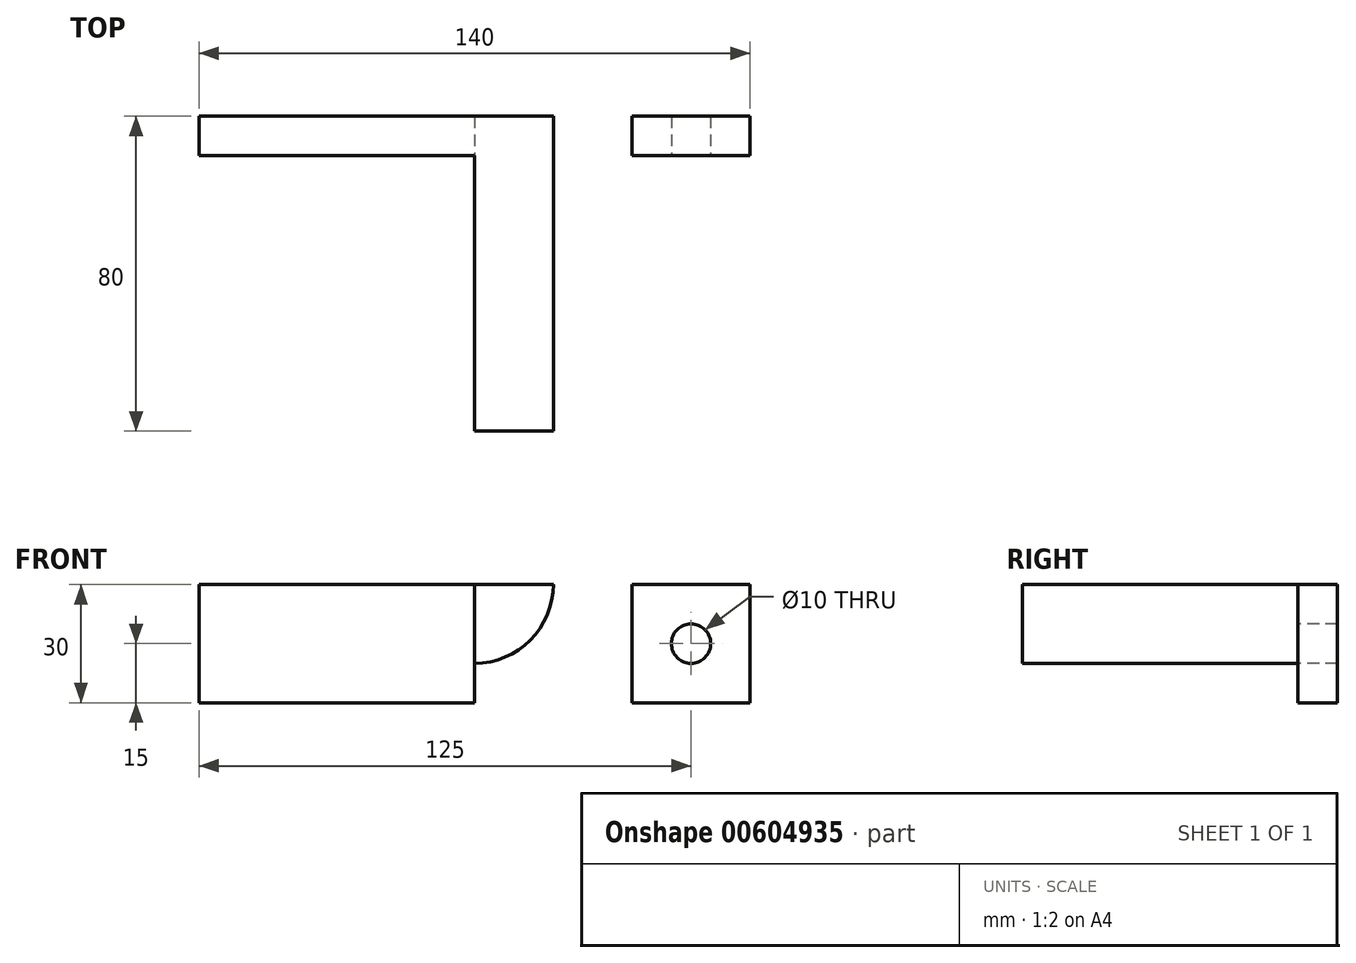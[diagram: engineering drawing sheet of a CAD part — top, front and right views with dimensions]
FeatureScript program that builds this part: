
annotation { "Feature Type Name" : "Feature", "Feature Type Description" : "" }
export const myFeature = defineFeature(function(context is Context, id is Id, definition is map)
    precondition{}
    {
        {
            var Q0;
            Q0=qCreatedBy(makeId("Right.planeOp"),FACE);
            var sketch = newSketch(context, id + "F0", { "sketchPlane" : qUnion([Q0])});
            skLineSegment(sketch, "E0", {"start": v(0, 30) * mm, "end": v(0, 0) * mm});
            skLineSegment(sketch, "E1", {"start": v(0, 0) * mm, "end": v(-60, 0) * mm});
            skLineSegment(sketch, "E2", {"start": v(-60, 0) * mm, "end": v(-60, -30) * mm});
            skLineSegment(sketch, "E3", {"start": v(-60, -30) * mm, "end": v(10, -30) * mm, "construction": true});
            skLineSegment(sketch, "E4", {"start": v(10, -30) * mm, "end": v(10, 30) * mm});
            skLineSegment(sketch, "E5", {"start": v(0, 30) * mm, "end": v(10, 30) * mm});
            skArc(sketch, "E6", {"start": v(-45, -30) * mm, "mid": v(-25, -10) * mm, "end": v(-5, -30) * mm});
            skLineSegment(sketch, "E7", {"start": v(-60, -30) * mm, "end": v(-45, -30) * mm, "construction": true});
            skLineSegment(sketch, "E8", {"start": v(-5, -30) * mm, "end": v(10, -30) * mm, "construction": true});
            skLineSegment(sketch, "E9", {"start": v(-60, -30) * mm, "end": v(-45, -30) * mm});
            skLineSegment(sketch, "E10", {"start": v(-5, -30) * mm, "end": v(10, -30) * mm});
            skSolve(sketch);
        }
        {
            var Q0;
            Q0=makeQuery(id+"F0.imprint","IMPRINT",FACE,{"disambiguationData":[TD([[makeQuery(id+"F0.imprint","IMPRINT",EDGE,{"derivedFrom":sQuery(id+"F0.wireOp",EDGE,"E0")}),1.0]])]});
            extrude(context, id + "F1", {"entities" : qUnion([Q0]), "endBound" : BoundingType.SYMMETRIC, "depth" : 140 * mm, "offsetDistance" : 25 * mm});
        }
        {
            var Q0;
            Q0=makeQuery(id+"F1.opExtrude","SWEPT_FACE",FACE,{"disambiguationData":[OSD([sQuery(id+"F0.wireOp",EDGE,"E0")])]});
            var sketch = newSketch(context, id + "F2", { "sketchPlane" : qUnion([Q0])});
            skLineSegment(sketch, "E11.bottom", {"start": v(40, 0) * mm, "end": v(0, 0) * mm});
            skLineSegment(sketch, "E11.top", {"start": v(40, 30) * mm, "end": v(0, 30) * mm});
            skLineSegment(sketch, "E11.left", {"start": v(40, 0) * mm, "end": v(40, 30) * mm});
            skLineSegment(sketch, "E11.right", {"start": v(0, 0) * mm, "end": v(0, 30) * mm});
            skSolve(sketch);
        }
        {
            var Q0;
            Q0=makeQuery(id+"F2.imprint","IMPRINT",FACE,{"disambiguationData":[TD([[makeQuery(id+"F2.imprint","IMPRINT",EDGE,{"derivedFrom":sQuery(id+"F2.wireOp",EDGE,"E11.bottom")}),-1.0]])]});
            extrude(context, id + "F3", {"entities" : qUnion([Q0]), "operationType" : NewBodyOperationType.ADD, "depth" : 60 * mm, "offsetDistance" : 25 * mm});
        }
        {
            var Q0;
            {var subQ0=sQuery(id+"F2.wireOp",EDGE,"E11.right");var subQ1=sQuery(id+"F2.wireOp",EDGE,"E11.left");var subQ2=sQuery(id+"F2.wireOp",EDGE,"E11.top");var subQ3=sQuery(id+"F2.wireOp",EDGE,"E11.bottom");Q0=makeQuery(id+"FlGcxx7yue9F5qh_1.1.F3.boolean.opBoolean","MERGE",FACE,{"derivedFrom":[makeQuery(id+"F3.boolean.opBoolean","MERGE",FACE,{"derivedFrom":[makeQuery(id+"F1.opExtrude","SWEPT_FACE",FACE,{"disambiguationData":[OSD([sQuery(id+"F0.wireOp",EDGE,"E2")])]}),makeQuery(id+"F3.opExtrude","CAP_FACE",FACE,{"disambiguationData":[OSD([subQ3,subQ2,subQ1,subQ0])],"isStart":false})]}),makeQuery(id+"FlGcxx7yue9F5qh_1.1.F3.opExtrude","CAP_FACE",FACE,{"disambiguationData":[OSD([subQ3,subQ2,subQ1,subQ0])],"isStart":false})]});}
            var sketch = newSketch(context, id + "F4", { "sketchPlane" : qUnion([Q0])});
            skArc(sketch, "E12", {"start": v(20, 30) * mm, "mid": v(0, 10) * mm, "end": v(-20, 30) * mm});
            skSolve(sketch);
        }
        {
            var Q0;
            {var subQ0=sQuery(id+"F4.wireOp",EDGE,"E12");Q0=makeQuery(id+"F4.imprint","IMPRINT",FACE,{"disambiguationData":[TD([[makeQuery(id+"F4.imprint","IMPRINT",EDGE,{"derivedFrom":subQ0}),-1.0]])]});}
            extrude(context, id + "F5", {"entities" : qUnion([Q0]), "operationType" : NewBodyOperationType.REMOVE, "endBound" : BoundingType.THROUGH_ALL, "oppositeDirection" : true, "depth" : 25 * mm, "offsetDistance" : 25 * mm});
        }
        {
            var Q0;
            {var subQ0=sQuery(id+"F2.wireOp",EDGE,"E11.right");var subQ1=sQuery(id+"F2.wireOp",EDGE,"E11.left");var subQ2=sQuery(id+"F2.wireOp",EDGE,"E11.top");var subQ3=sQuery(id+"F2.wireOp",EDGE,"E11.bottom");Q0=makeQuery(id+"FlGcxx7yue9F5qh_1.1.F3.boolean.opBoolean","MERGE",FACE,{"derivedFrom":[makeQuery(id+"F3.boolean.opBoolean","MERGE",FACE,{"derivedFrom":[makeQuery(id+"F1.opExtrude","SWEPT_FACE",FACE,{"disambiguationData":[OSD([sQuery(id+"F0.wireOp",EDGE,"E2")])]}),makeQuery(id+"F3.opExtrude","CAP_FACE",FACE,{"disambiguationData":[OSD([subQ3,subQ2,subQ1,subQ0])],"isStart":false})]}),makeQuery(id+"FlGcxx7yue9F5qh_1.1.F3.opExtrude","CAP_FACE",FACE,{"disambiguationData":[OSD([subQ3,subQ2,subQ1,subQ0])],"isStart":false})]});}
            var sketch = newSketch(context, id + "F6", { "sketchPlane" : qUnion([Q0])});
            skArc(sketch, "E13.0", {"start": v(20, 30) * mm, "mid": v(0, 10) * mm, "end": v(-20, 30) * mm});
            skArc(sketch, "E14", {"start": v(30, 30) * mm, "mid": v(0, 0) * mm, "end": v(-30, 30) * mm});
            skSolve(sketch);
        }
        {
            var Q0;
            {var subQ0=sQuery(id+"F6.wireOp",EDGE,"E13.0");Q0=makeQuery(id+"F6.imprint","IMPRINT",FACE,{"disambiguationData":[TD([[makeQuery(id+"F6.imprint","IMPRINT",EDGE,{"derivedFrom":subQ0}),1.0]])]});}
            extrude(context, id + "F7", {"entities" : qUnion([Q0]), "operationType" : NewBodyOperationType.ADD, "depth" : 10 * mm, "offsetDistance" : 25 * mm});
        }
        {
            var Q0;
            Q0=qCreatedBy(makeId("Front.planeOp"),FACE);
            var sketch = newSketch(context, id + "F8", { "sketchPlane" : qUnion([Q0])});
            skCircle(sketch, "E15", {"center": v(55, 15) * mm, "radius": 5 * mm});
            skSolve(sketch);
        }
        {
            var Q0;
            Q0=makeQuery(id+"F8.imprint","IMPRINT",FACE,{"disambiguationData":[TD([[makeQuery(id+"F8.imprint","IMPRINT",EDGE,{"derivedFrom":sQuery(id+"F8.wireOp",EDGE,"E15")}),1.0]])]});
            extrude(context, id + "F9", {"entities" : qUnion([Q0]), "operationType" : NewBodyOperationType.REMOVE, "endBound" : BoundingType.THROUGH_ALL, "oppositeDirection" : true, "depth" : 25 * mm, "offsetDistance" : 25 * mm});
        }
    });
